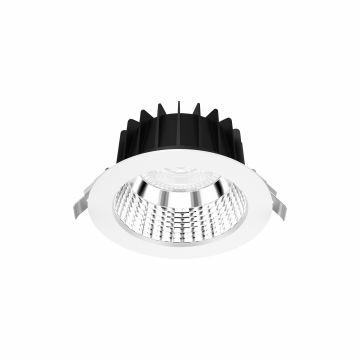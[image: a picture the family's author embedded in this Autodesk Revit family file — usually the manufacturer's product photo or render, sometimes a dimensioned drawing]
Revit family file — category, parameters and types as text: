
# Revit family: Lighting-CommercialSector-GEWISS-ELIA-AL-LED_ACCENT_D172
name_source: partatom
category: Apparecchi per illuminazione
units: mm (PartAtom-declared; Revit-internal decimal feet)

## family parameters
Condiviso = No
Host = Superficie
Punto di calcolo locali = Sì
Quota connettore circolare = Usa diametro
Sorgente d'illuminazione = Sì
Taglio con vuoti quando caricato = No
Tipo di parte = Normale

## types (16) — shared parameters
Angolo inclinazione = -90.00°
Application = Indoor
Catalogue = LIGHTING
Catalogue Range = ELIA AL
Colour = White
Dimensions (mm) = Standard
Emetti da lunghezza linea = 610 mm
FORO_CONTROSOFFITTO = 80 mm  [stored 0.262467 ft]
File diagramma fotometrico = GWF1411MH940.IES
Filtro dei colori = 16777215
IDF = da994d68-7c15-409b-becf-5cf5e9cdf8f4
IDT = c1be2df2-232f-40c1-8cd1-aa0a19295d6b
IP degree = IP40 - IP54
Immagine tipo = ELIA_AL.jpg
Installation = Flush mounted
Insulation class = II
LARGHEZZA_FORO = 820 mm
LED = <Per categoria>
LED Life time (L80B50) = L80 B50 (Tq25°) = 50.000h
LUNGHEZZA FORO = 969 mm
L_lampada = 1500 mm
Lamp = LED
Operating temperature: = -20° +45°
POSIZIONE = 80000
Produttore = GEWISS S.p.A.
Prospetto di default = 1219 mm
SEO = Flush mounted
STRUTTURA = <Per categoria>
Shock resistance = IK06
System power = 25W
Technical sheet = https://www.gewiss.com
Type of lamp = LED
Type of light source = LED - Not replaceable
Typology = Flush mounted
UGR: = UGR<19
URL = https://www.gewiss.com
Variazione temperatura colore lampada con luminosità attenuata = <Nessuno>
Version file RFA = 20.0
Voltage = 220-240 VÂ
Warranty = 5 years
Weight (kg) = 0,7
Weight (kg): = 0,7
Working temperature = -20° +45°

## per-type parameters (varying)
| type | Colour temperature | Colour temperature: | Descrizione | Lumen output (lm) | Modello | Optic |
| GWF1410MG940 - ELIA AL M2 40K 36° ST.ALONE ON/OFF CRI90 | 4000K | 4000K | ELIA AL M2 40K 36° ST.ALONE ON/OFF CRI90 | 2430 | GWF1410MG940 | 36° |
| GWF1410MG930 - ELIA AL M2 30K 36° ST.ALONE ON/OFF CRI90 | 3000K | 3000K | ELIA AL M2 30K 36° ST.ALONE ON/OFF CRI90 | 2250 | GWF1410MG930 | 36° |
| GWF1410MH840 - ELIA AL M2 40K 60° ST.ALONE ON/OFF CRI80 | 4000K | 4000K | ELIA AL M2 40K 60° ST.ALONE ON/OFF CRI80 | 2840 | GWF1410MH840 | 60° |
| GWF1410MH930 - ELIA AL M2 30K 60° ST.ALONE ON/OFF CRI90 | 3000K | 3000K | ELIA AL M2 30K 60° ST.ALONE ON/OFF CRI90 | 2340 | GWF1410MH930 | 60° |
| GWF1410MH830 - ELIA AL M2 30K 60° ST.ALONE ON/OFF CRI80 | 3000K | 3000K | ELIA AL M2 30K 60° ST.ALONE ON/OFF CRI80 | 2600 | GWF1410MH830 | 60° |
| GWF1411MH840 - ELIA AL M2 40K 60° ST.ALONE DALI CRI80 | 4000K | 4000K | ELIA AL M2 40K 60° ST.ALONE DALI CRI80 | 2840 | GWF1411MH840 | 60° |
| GWF1410MH940 - ELIA AL M2 40K 60° ST.ALONE ON/OFF CRI90 | 4000K | 4000K | ELIA AL M2 40K 60° ST.ALONE ON/OFF CRI90 | 2550 | GWF1410MH940 | 60° |
| GWF1411MG830 - ELIA AL M2 30K 36° ST.ALONE DALI CRI80 | 3000K | 3000K | ELIA AL M2 30K 36° ST.ALONE DALI CRI80 | 2500 | GWF1411MG830 | 36° |
| GWF1410MG830 - ELIA AL M2 30K 36° ST.ALONE ON/OFF CRI80 | 3000K | 3000K | ELIA AL M2 30K 36° ST.ALONE ON/OFF CRI80 | 2500 | GWF1410MG830 | 36° |
| GWF1411MG840 - ELIA AL M2 40K 36° ST.ALONE DALI CRI80 | 4000K | 4000K | ELIA AL M2 40K 36° ST.ALONE DALI CRI80 | 2700 | GWF1411MG840 | 36° |
| GWF1411MG930 - ELIA AL M2 30K 36° ST.ALONE DALI CRI90 | 3000K | 3000K | ELIA AL M2 30K 36° ST.ALONE DALI CRI90 | 2250 | GWF1411MG930 | 36° |
| GWF1411MG940 - ELIA AL M2 40K 36° ST.ALONE DALI CRI90 | 4000K | 4000K | ELIA AL M2 40K 36° ST.ALONE DALI CRI90 | 2430 | GWF1411MG940 | 36° |
| GWF1411MH940 - ELIA AL M2 40K 60° ST.ALONE DALI CRI90 | 4000K | 4000K | ELIA AL M2 40K 60° ST.ALONE DALI CRI90 | 2550 | GWF1411MH940 | 60° |
| GWF1410MG840 - ELIA AL M2 40K 36° ST.ALONE ON/OFF CRI80 | 4000K | 4000K | ELIA AL M2 40K 36° ST.ALONE ON/OFF CRI80 | 2700 | GWF1410MG840 | 36° |
| GWF1411MH930 - ELIA AL M2 30K 60° ST.ALONE DALI CRI90 | 3000K | 3000K | ELIA AL M2 30K 60° ST.ALONE DALI CRI90 | 2340 | GWF1411MH930 | 60° |
| GWF1411MH830 - ELIA AL M2 30K 60° ST.ALONE DALI CRI80 | 3000K | 3000K | ELIA AL M2 30K 60° ST.ALONE DALI CRI80 | 2600 | GWF1411MH830 | 60° |

note: [stored X ft] marks values corroborated as IEEE doubles in the binary element streams (Revit-internal decimal feet)
